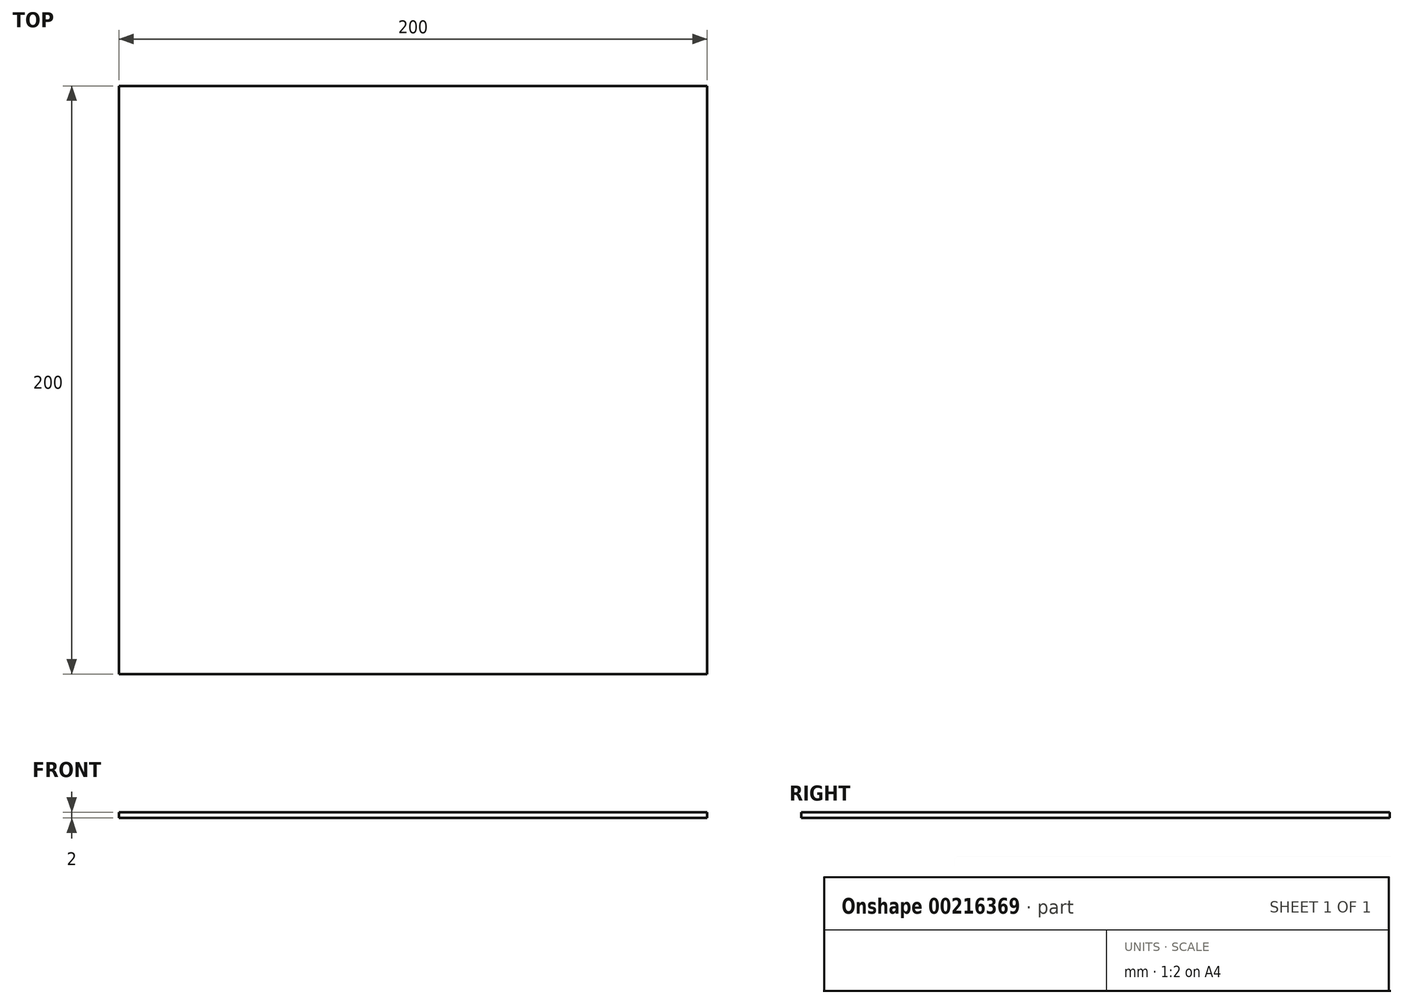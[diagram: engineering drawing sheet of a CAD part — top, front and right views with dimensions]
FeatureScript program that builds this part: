
annotation { "Feature Type Name" : "Feature", "Feature Type Description" : "" }
export const myFeature = defineFeature(function(context is Context, id is Id, definition is map)
    precondition{}
    {
        {
            var Q0;
            Q0=qCreatedBy(makeId("Top.planeOp"),FACE);
            var sketch = newSketch(context, id + "F0", { "sketchPlane" : qUnion([Q0])});
            skLineSegment(sketch, "E0.bottom", {"start": v(-167.38, 142.17) * mm, "end": v(32.62, 142.17) * mm});
            skLineSegment(sketch, "E0.top", {"start": v(-167.38, -57.83) * mm, "end": v(32.62, -57.83) * mm});
            skLineSegment(sketch, "E0.left", {"start": v(-167.38, 142.17) * mm, "end": v(-167.38, -57.83) * mm});
            skLineSegment(sketch, "E0.right", {"start": v(32.62, 142.17) * mm, "end": v(32.62, -57.83) * mm});
            skSolve(sketch);
        }
        {
            var Q0;
            Q0 = qSketchRegion(id + "F0", true);
            extrude(context, id + "F1", {"entities" : qUnion([Q0]), "depth" : 2 * mm, "offsetDistance" : 25 * mm});
        }
    });
